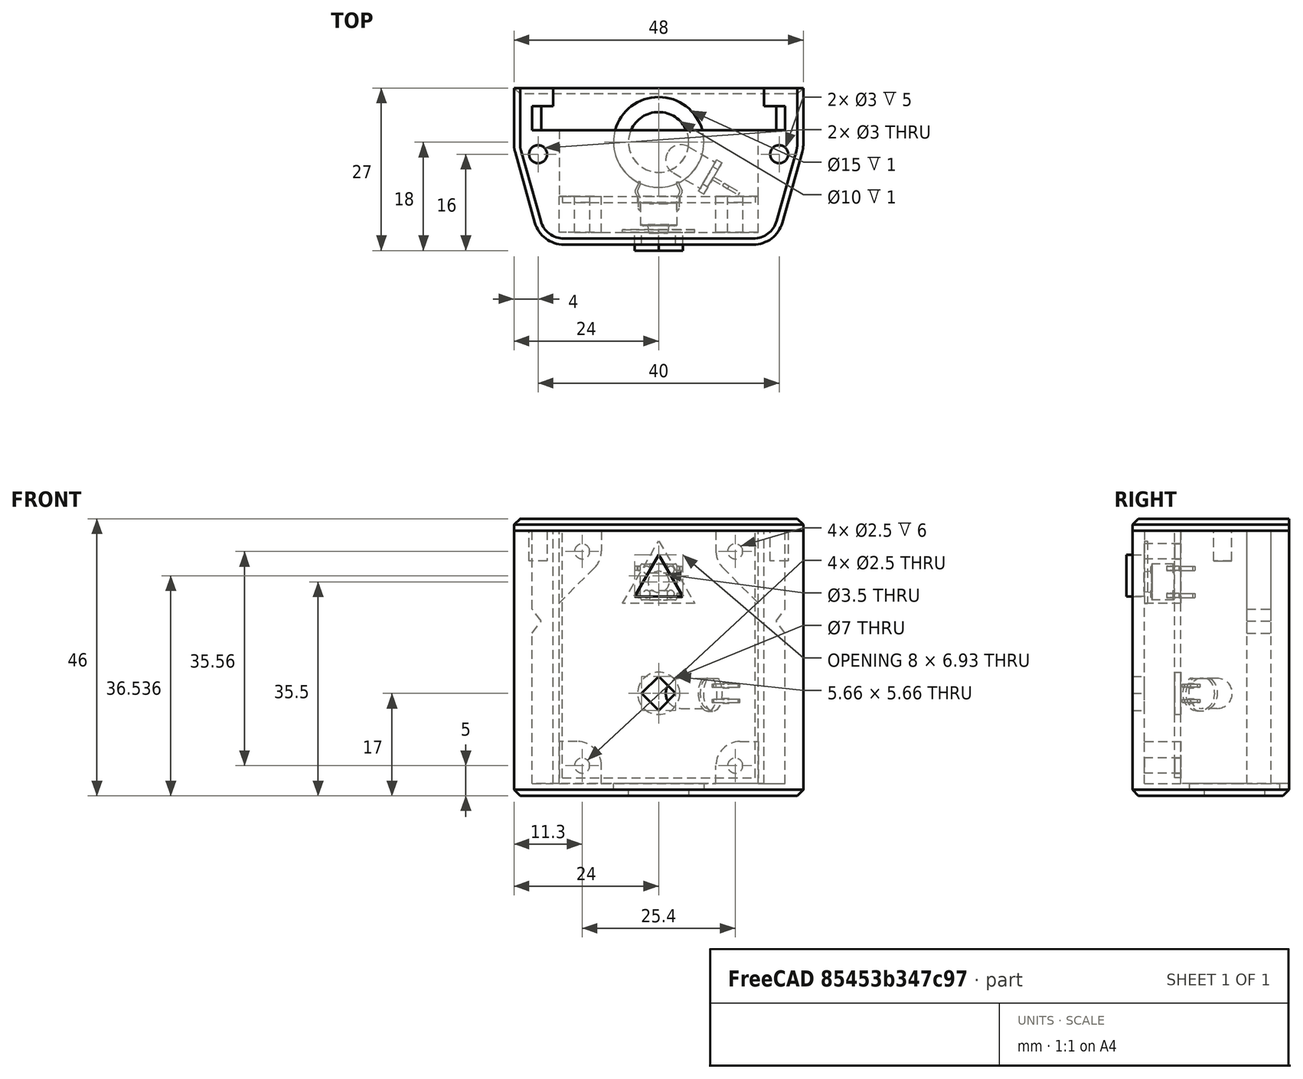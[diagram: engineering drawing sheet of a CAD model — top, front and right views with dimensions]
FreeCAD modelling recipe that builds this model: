
FCSTD DOCUMENT  (FreeCAD 2023.114R26244 +5346 (Git))
Label: avvisoBoule
License: All rights reserved
LicenseURL: http://en.wikipedia.org/wiki/All_rights_reserved
objects: Sketcher::SketchObject×12, PartDesign::Pad×7, PartDesign::Pocket×5, Part::SubShapeBinder×4, PartDesign::Body×4, App::Part×4, PartDesign::Fillet×3, Part::Feature×3, PartDesign::Chamfer×2, PartDesign::AdditiveBox×1, Mesh::Feature×1
note: 89 computed .brp shape members not serialized (recipe doc carries the construction recipe); baked Part::Feature solids carry a one-line shape summary decoded from their .brp

FEATURE [Sketcher::SketchObject] Sketch
  ArcFitTolerance = 1e-06
  AttachmentSupport = -> [XY_Plane]
  ExternalBSplineMaxDegree = 5
  ExternalBSplineTolerance = 0.0001
  FullyConstrained = true
  InternalTolerance = 1e-06
  InvalidShape = false
  MakeInternals = false
  MapMode = 5
  Support = -> [XY_Plane]
  TreeRank = 18
  ValidateShape = true
  sketch-geometry (18):
    g0: LineSegment StartX=-17.5 StartY=4 StartZ=0 EndX=-17.5 EndY=7 EndZ=0
    g1: LineSegment StartX=-17.5 StartY=7 StartZ=0 EndX=-24 EndY=7 EndZ=0
    g2: LineSegment StartX=-24 StartY=7 StartZ=0 EndX=-24 EndY=-3 EndZ=0
    g3: LineSegment StartX=24 StartY=-3 StartZ=0 EndX=24 EndY=7 EndZ=0
    g4: LineSegment StartX=24 StartY=7 StartZ=0 EndX=17.5 EndY=7 EndZ=0
    g5: LineSegment StartX=17.5 StartY=7 StartZ=0 EndX=17.5 EndY=4 EndZ=0
    g6: LineSegment StartX=17.5 StartY=4 StartZ=0 EndX=21 EndY=4 EndZ=0
    g7: LineSegment StartX=21 StartY=4 StartZ=0 EndX=21 EndY=0 EndZ=0
    g8: LineSegment StartX=-21 StartY=0 StartZ=0 EndX=-21 EndY=4 EndZ=0
    g9: LineSegment StartX=-21 StartY=4 StartZ=0 EndX=-17.5 EndY=4 EndZ=0
    g10: LineSegment StartX=-19.5 StartY=-19 StartZ=0 EndX=19.5 EndY=-19 EndZ=0
    g11: LineSegment StartX=-16.5 StartY=0 StartZ=0 EndX=-16.5 EndY=-17 EndZ=0
    g12: LineSegment StartX=-16.5 StartY=-17 StartZ=0 EndX=16.5 EndY=-17 EndZ=0
    g13: LineSegment StartX=16.5 StartY=-17 StartZ=0 EndX=16.5 EndY=0 EndZ=0
    g14: LineSegment StartX=-16.5 StartY=0 StartZ=0 EndX=-21 EndY=0 EndZ=0
    g15: LineSegment StartX=16.5 StartY=0 StartZ=0 EndX=21 EndY=0 EndZ=0
    g16: LineSegment StartX=-24 StartY=-3 StartZ=0 EndX=-19.5 EndY=-19 EndZ=0
    g17: LineSegment StartX=19.5 StartY=-19 StartZ=0 EndX=24 EndY=-3 EndZ=0
  constraints (51):
    c: Vertical(g0)
    c: Coincident(g0,g1)
    c: Coincident(g1,g2)
    c: Vertical(g2)
    c: Coincident(g3,g4)
    c: Coincident(g4,g5)
    c: Coincident(g5,g6)
    c: Coincident(g6,g7)
    c: Coincident(g14,g8)
    c: Vertical(g8)
    c: Coincident(g8,g9)
    c: Coincident(g9,g0)
    c: Horizontal(g9)
    c: Horizontal(g1)
    c: Horizontal(g4)
    c: Horizontal(g6)
    c: Vertical(g3)
    c: Vertical(g7)
    c: Vertical(g5)
    c: Equal(g4,g1)
    c: Equal(g6,g9)
    c: Equal(g0,g5)
    c: Symmetric(g0,g4,g-2)
    c: PointOnObject(g14,g-1)
    c: DistanceY(g2,g14) = 3
    c: DistanceY(g8,g8) = 4
    c: DistanceX(g0,g4) = 35
    c: DistanceX(g14,g7) = 42
    c: DistanceX(g1,g8) = 3
    c: DistanceY(g0,g0) = 3
    c: Symmetric(g10,g10,g-2)
    c: Vertical(g11)
    c: Coincident(g11,g12)
    c: Coincident(g12,g13)
    c: Vertical(g13)
    c: Coincident(g14,g11)
    c: Symmetric(g11,g12,g-2)
    c: Coincident(g15,g13)
    c: Coincident(g15,g7)
    c: Coincident(g16,g2)
    c: Coincident(g16,g10)
    c: Coincident(g17,g10)
    c: Coincident(g17,g3)
    c: DistanceX(g14,g14) = 4.5
    c: DistanceY(g11,g11) = 17
    c: Horizontal(g14)
    c: DistanceY(g10,g11) = 2
    c: DistanceX(g10,g11) = 3
    c: Equal(g7,g8)
    c: Horizontal(g15)
    c: Equal(g2,g3)
FEATURE [PartDesign::Pad] Pad
  AddSubType = 0
  AlongSketchNormal = false
  AutoTaperInnerAngle = true
  CheckUpToFaceLimits = true
  ClaimChildren = false
  Direction = (0,0,1)
  Fit = 0
  FitJoin = 0
  InnerFit = 0
  InnerFitJoin = 0
  InvalidShape = false
  Length = 42
  Length2 = 100
  Linearize = true
  NewSolid = false
  Profile = -> Sketch
  Suppress = false
  TaperInnerAngle = 0
  TaperInnerAngleRev = 0
  TreeRank = 19
  Type = 0
  ValidateShape = true
  _ProfileBasedVersion = 1
FEATURE [Sketcher::SketchObject] Sketch001
  ArcFitTolerance = 1e-06
  AttachmentSupport = -> [Pad]
  ExternalBSplineMaxDegree = 5
  ExternalBSplineTolerance = 0.0001
  ExternalGeometry = -> [Pad]
  FullyConstrained = true
  InternalTolerance = 1e-06
  InvalidShape = false
  MakeInternals = false
  MapMode = 5
  Placement = pos=(0,0,0) rot=(1,0,0;3.14159rad)
  Support = -> [Pad]
  TreeRank = 20
  ValidateShape = true
  sketch-geometry (6):
    g0: LineSegment StartX=-19.5 StartY=19 StartZ=0 EndX=19.5 EndY=19 EndZ=0
    g1: LineSegment StartX=19.5 StartY=19 StartZ=0 EndX=24 EndY=3 EndZ=0
    g2: LineSegment StartX=24 StartY=3 StartZ=0 EndX=24 EndY=-7 EndZ=0
    g3: LineSegment StartX=24 StartY=-7 StartZ=0 EndX=-24 EndY=-7 EndZ=0
    g4: LineSegment StartX=-24 StartY=-7 StartZ=0 EndX=-24 EndY=3 EndZ=0
    g5: LineSegment StartX=-24 StartY=3 StartZ=0 EndX=-19.5 EndY=19 EndZ=0
  constraints (12):
    c: Coincident(g-3,g0)
    c: Coincident(g0,g-3)
    c: Coincident(g0,g1)
    c: Coincident(g1,g-5)
    c: Coincident(g1,g2)
    c: Coincident(g2,g-5)
    c: Coincident(g2,g3)
    c: Coincident(g3,g-4)
    c: Coincident(g3,g4)
    c: Coincident(g4,g-4)
    c: Coincident(g4,g5)
    c: Coincident(g5,g0)
FEATURE [PartDesign::Pad] Pad001
  AddSubType = 0
  AlongSketchNormal = false
  AutoTaperInnerAngle = true
  BaseFeature = -> Pad
  CheckUpToFaceLimits = true
  ClaimChildren = false
  Direction = (0,0,-1)
  Fit = 0
  FitJoin = 0
  InnerFit = 0
  InnerFitJoin = 0
  InvalidShape = false
  Length = 2
  Length2 = 100
  Linearize = true
  NewSolid = false
  Profile = -> Sketch001
  Suppress = false
  TaperInnerAngle = 0
  TaperInnerAngleRev = 0
  TreeRank = 21
  Type = 0
  ValidateShape = true
  _ProfileBasedVersion = 1
FEATURE [Sketcher::SketchObject] Sketch002
  ArcFitTolerance = 1e-06
  AttachmentSupport = -> [Pad001]
  ExternalBSplineMaxDegree = 5
  ExternalBSplineTolerance = 0.0001
  FullyConstrained = true
  InternalTolerance = 1e-06
  InvalidShape = false
  MakeInternals = false
  MapMode = 5
  Placement = pos=(0,-19,0) rot=(1,0,0;1.5708rad)
  Support = -> [Pad001]
  TreeRank = 22
  ValidateShape = true
  sketch-geometry (7):
    g0: LineSegment StartX=-4 StartY=31.0718 StartZ=0 EndX=-4.459e-13 EndY=38 EndZ=0
    g1: LineSegment StartX=-4.46e-13 StartY=38 StartZ=0 EndX=4 EndY=31.0718 EndZ=0
    g2: LineSegment StartX=-2.82843 StartY=15 StartZ=0 EndX=0 EndY=17.8284 EndZ=0
    g3: LineSegment StartX=0 StartY=17.8284 StartZ=0 EndX=2.82843 EndY=15 EndZ=0
    g4: LineSegment StartX=2.82843 StartY=15 StartZ=0 EndX=0 EndY=12.1716 EndZ=0
    g5: LineSegment StartX=0 StartY=12.1716 StartZ=0 EndX=-2.82843 EndY=15 EndZ=0
    g6: LineSegment StartX=-4 StartY=31.0718 StartZ=0 EndX=4 EndY=31.0718 EndZ=0
  constraints (20):
    c: Coincident(g0,g1)
    c: Symmetric(g0,g1,g-2)
    c: Angle(g0,g1) = 1.0472
    c: Coincident(g2,g3)
    c: Coincident(g3,g4)
    c: Coincident(g4,g5)
    c: Coincident(g5,g2)
    c: Parallel(g5,g3)
    c: Parallel(g2,g4)
    c: PointOnObject(g2,g-2)
    c: PointOnObject(g4,g-2)
    c: Horizontal(g2,g3)
    c: Angle(g2,g3) = 1.5708
    c: DistanceY(g2) = 15
    c: Distance(g4) = 4
    c: Distance(g0) = 8
    c: Equal(g1,g0)
    c: Coincident(g6,g0)
    c: Coincident(g6,g1)
    c: DistanceY(g0) = 38
FEATURE [PartDesign::Pocket] Pocket
  AddSubType = 1
  AutoTaperInnerAngle = true
  BaseFeature = -> Pad001
  CheckUpToFaceLimits = true
  ClaimChildren = false
  Fit = 0
  FitJoin = 0
  InnerFit = 0
  InnerFitJoin = 0
  InvalidShape = false
  Length = 5
  Length2 = 100
  Linearize = true
  NewSolid = false
  Profile = -> Sketch002
  Suppress = false
  TaperInnerAngle = 0
  TaperInnerAngleRev = 0
  TreeRank = 23
  Type = 2
  ValidateShape = true
  _ProfileBasedVersion = 1
  _Version = 1
FEATURE [Sketcher::SketchObject] Sketch003
  ArcFitTolerance = 1e-06
  AttachmentSupport = -> [Pocket]
  ExternalBSplineMaxDegree = 5
  ExternalBSplineTolerance = 0.0001
  ExternalGeometry = -> [Pocket]
  FullyConstrained = true
  InternalTolerance = 1e-06
  InvalidShape = false
  MakeInternals = false
  MapMode = 5
  Placement = pos=(0,0,0) rot=(0,0.707107,0.707107;3.14159rad)
  Support = -> [Pocket]
  TreeRank = 24
  ValidateShape = true
  sketch-geometry (6):
    g0: LineSegment StartX=-21 StartY=29 StartZ=0 EndX=-21 EndY=25 EndZ=0
    g1: LineSegment StartX=-21 StartY=25 StartZ=0 EndX=-19.5 EndY=27 EndZ=0
    g2: LineSegment StartX=-19.5 StartY=27 StartZ=0 EndX=-21 EndY=29 EndZ=0
    g3: LineSegment StartX=21 StartY=29 StartZ=0 EndX=21 EndY=25 EndZ=0
    g4: LineSegment StartX=21 StartY=25 StartZ=0 EndX=19.5 EndY=27 EndZ=0
    g5: LineSegment StartX=19.5 StartY=27 StartZ=0 EndX=21 EndY=29 EndZ=0
  constraints (17):
    c: PointOnObject(g0,g-3)
    c: PointOnObject(g0,g-3)
    c: Coincident(g0,g1)
    c: Coincident(g1,g2)
    c: Coincident(g2,g0)
    c: PointOnObject(g3,g-4)
    c: PointOnObject(g3,g-4)
    c: Coincident(g3,g4)
    c: Coincident(g4,g5)
    c: Coincident(g5,g3)
    c: Horizontal(g0,g3)
    c: Equal(g0,g3)
    c: Symmetric(g1,g4,g-2)
    c: DistanceX(g0,g1) = 1.5
    c: DistanceY(g0,g0) = 4
    c: DistanceY(g0,g1) = 2
    c: DistanceY(g0) = 25
FEATURE [PartDesign::Pad] Pad002
  AddSubType = 0
  AlongSketchNormal = false
  AutoTaperInnerAngle = true
  BaseFeature = -> Pocket
  CheckUpToFaceLimits = true
  ClaimChildren = false
  Direction = (0,1,-2e-16)
  Fit = 0
  FitJoin = 0
  InnerFit = 0
  InnerFitJoin = 0
  InvalidShape = false
  Length = 10
  Length2 = 100
  Linearize = true
  NewSolid = false
  Profile = -> Sketch003
  Suppress = false
  TaperInnerAngle = 0
  TaperInnerAngleRev = 0
  TreeRank = 25
  Type = 3
  UpToFace = -> Pocket [Face10]
  ValidateShape = true
  _ProfileBasedVersion = 1
FEATURE [PartDesign::Fillet] Fillet
  AddSubType = 0
  Base = -> Pad002 [Edge72,Edge74,Edge77,Edge85]
  BaseFeature = -> Pad002
  InvalidShape = false
  NewSolid = false
  Radius = 5
  SupportTransform = false
  Suppress = false
  TreeRank = 26
  ValidateShape = true
FEATURE [Sketcher::SketchObject] Sketch004
  ArcFitTolerance = 1e-06
  AttachmentSupport = -> [Fillet]
  ExternalBSplineMaxDegree = 5
  ExternalBSplineTolerance = 0.0001
  ExternalGeometry = -> [Fillet]
  FullyConstrained = true
  InternalTolerance = 1e-06
  InvalidShape = false
  MakeInternals = false
  MapMode = 5
  Placement = pos=(0,-17,0) rot=(0,0.707107,0.707107;3.14159rad)
  Support = -> [Fillet]
  TreeRank = 27
  ValidateShape = true
  sketch-geometry (20):
    g0: LineSegment StartX=-16.5 StartY=42 StartZ=0 EndX=-9.5 EndY=42 EndZ=0
    g1: LineSegment StartX=-9.5 StartY=42 StartZ=0 EndX=-9.5 EndY=37 EndZ=0
    g2: LineSegment StartX=-16.5 StartY=30 StartZ=0 EndX=-16.5 EndY=42 EndZ=0
    g3: LineSegment StartX=16.5 StartY=42 StartZ=0 EndX=9.5 EndY=42 EndZ=0
    g4: LineSegment StartX=9.5 StartY=42 StartZ=0 EndX=9.5 EndY=37 EndZ=0
    g5: LineSegment StartX=16.5 StartY=30 StartZ=0 EndX=16.5 EndY=42 EndZ=0
    g6: LineSegment StartX=-16.5 StartY=0 StartZ=0 EndX=-9.5 EndY=0 EndZ=0
    g7: LineSegment StartX=-9.5 StartY=0 StartZ=0 EndX=-9.5 EndY=7 EndZ=0
    g8: LineSegment StartX=-9.5 StartY=7 StartZ=0 EndX=-16.5 EndY=7 EndZ=0
    g9: LineSegment StartX=-16.5 StartY=7 StartZ=0 EndX=-16.5 EndY=0 EndZ=0
    g10: LineSegment StartX=16.5 StartY=0 StartZ=0 EndX=9.5 EndY=0 EndZ=0
    g11: LineSegment StartX=9.5 StartY=0 StartZ=0 EndX=9.5 EndY=7 EndZ=0
    g12: LineSegment StartX=9.5 StartY=7 StartZ=0 EndX=16.5 EndY=7 EndZ=0
    g13: LineSegment StartX=16.5 StartY=7 StartZ=0 EndX=16.5 EndY=0 EndZ=0
    g14: Circle CenterX=-12.7 CenterY=38.56 CenterZ=0 NormalX=0 NormalY=0 NormalZ=1 AngleXU=0 Radius=1.25
    g15: Circle CenterX=-12.7 CenterY=3 CenterZ=0 NormalX=0 NormalY=0 NormalZ=1 AngleXU=0 Radius=1.25
    g16: Circle CenterX=12.7 CenterY=3 CenterZ=0 NormalX=0 NormalY=0 NormalZ=1 AngleXU=0 Radius=1.25
    g17: Circle CenterX=12.7 CenterY=38.56 CenterZ=0 NormalX=0 NormalY=0 NormalZ=1 AngleXU=0 Radius=1.25
    g18: LineSegment StartX=-16.5 StartY=30 StartZ=0 EndX=-9.5 EndY=37 EndZ=0
    g19: LineSegment StartX=9.5 StartY=37 StartZ=0 EndX=16.5 EndY=30 EndZ=0
  constraints (55):
    c: Coincident(g0,g1)
    c: Coincident(g2,g0)
    c: Horizontal(g0)
    c: Vertical(g1)
    c: Vertical(g2)
    c: Coincident(g3,g4)
    c: Coincident(g5,g3)
    c: Horizontal(g3)
    c: Vertical(g4)
    c: Vertical(g5)
    c: Coincident(g6,g7)
    c: Coincident(g7,g8)
    c: Coincident(g8,g9)
    c: Coincident(g9,g6)
    c: Horizontal(g6)
    c: Horizontal(g8)
    c: Vertical(g7)
    c: Vertical(g9)
    c: Coincident(g10,g11)
    c: Coincident(g11,g12)
    c: Coincident(g12,g13)
    c: Coincident(g13,g10)
    c: Horizontal(g10)
    c: Horizontal(g12)
    c: Vertical(g11)
    c: Vertical(g13)
    c: Equal(g8,g7)
    c: Equal(g1,g4)
    c: Equal(g12,g11)
    c: DistanceY(g7,g7) = 7
    c: Equal(g14,g17)
    c: Equal(g17,g16)
    c: Equal(g16,g15)
    c: Horizontal(g14,g17)
    c: Vertical(g14,g15)
    c: Diameter(g14) = 2.5
    c: DistanceY(g6,g15) = 3
    c: Vertical(g17,g16)
    c: DistanceX(g14,g17) = 25.4
    c: Symmetric(g16,g15,g-2)
    c: Coincident(g6,g-3)
    c: Coincident(g-3,g10)
    c: Coincident(g0,g-4)
    c: DistanceY(g15,g14) = 35.56
    c: Coincident(g18,g2)
    c: Coincident(g18,g1)
    c: Equal(g5,g2)
    c: Coincident(g3,g-4)
    c: Coincident(g19,g4)
    c: Coincident(g19,g5)
    c: Angle(g18) = 0.785398
    c: Vertical(g0,g7)
    c: Vertical(g3,g11)
    c: DistanceY(g1,g1) = 5
    c: Equal(g12,g8)
FEATURE [PartDesign::Pad] Pad003
  AddSubType = 0
  AlongSketchNormal = false
  AutoTaperInnerAngle = true
  BaseFeature = -> Fillet
  CheckUpToFaceLimits = true
  ClaimChildren = false
  Direction = (0,1,-2e-16)
  Fit = 0
  FitJoin = 0
  InnerFit = 0
  InnerFitJoin = 0
  InvalidShape = false
  Length = 6
  Length2 = 100
  Linearize = true
  NewSolid = false
  Profile = -> Sketch004
  Refine = true
  Suppress = false
  TaperInnerAngle = 0
  TaperInnerAngleRev = 0
  TreeRank = 28
  Type = 0
  ValidateShape = true
  _ProfileBasedVersion = 1
FEATURE [PartDesign::Fillet] Fillet001
  AddSubType = 0
  Base = -> Pad003 [Edge157,Edge154,Edge145,Edge146]
  BaseFeature = -> Pad003
  InvalidShape = false
  NewSolid = false
  Radius = 4
  SupportTransform = false
  Suppress = false
  TreeRank = 29
  ValidateShape = true
FEATURE [Sketcher::SketchObject] Sketch005
  ArcFitTolerance = 1e-06
  AttachmentSupport = -> [Fillet001]
  ExternalBSplineMaxDegree = 5
  ExternalBSplineTolerance = 0.0001
  FullyConstrained = true
  InternalTolerance = 1e-06
  InvalidShape = false
  MakeInternals = false
  MapMode = 5
  Support = -> [Fillet001]
  TreeRank = 30
  ValidateShape = true
  sketch-geometry (1):
    g0: Circle CenterX=0 CenterY=-2 CenterZ=0 NormalX=0 NormalY=0 NormalZ=1 AngleXU=0 Radius=7.5
  constraints (3):
    c: Diameter(g0) = 15
    c: PointOnObject(g0,g-2)
    c: DistanceY(g0) = -2
FEATURE [PartDesign::Pocket] Pocket001
  AddSubType = 1
  AutoTaperInnerAngle = true
  BaseFeature = -> Fillet001
  CheckUpToFaceLimits = true
  ClaimChildren = false
  Fit = 0
  FitJoin = 0
  InnerFit = 0
  InnerFitJoin = 0
  InvalidShape = false
  Length = 1
  Length2 = 100
  Linearize = true
  NewSolid = false
  Profile = -> Sketch005
  Suppress = false
  TaperInnerAngle = 0
  TaperInnerAngleRev = 0
  TreeRank = 31
  Type = 0
  ValidateShape = true
  _ProfileBasedVersion = 1
  _Version = 1
FEATURE [Sketcher::SketchObject] Sketch006
  ArcFitTolerance = 1e-06
  AttachmentSupport = -> [Pocket001]
  ExternalBSplineMaxDegree = 5
  ExternalBSplineTolerance = 0.0001
  ExternalGeometry = -> [Pocket001]
  FullyConstrained = true
  InternalTolerance = 1e-06
  InvalidShape = false
  MakeInternals = false
  MapMode = 5
  Placement = pos=(0,0,-1) rot=(0,0,1;0rad)
  Support = -> [Pocket001]
  TreeRank = 32
  ValidateShape = true
  sketch-geometry (1):
    g0: Circle CenterX=0 CenterY=-2 CenterZ=0 NormalX=0 NormalY=0 NormalZ=1 AngleXU=0 Radius=5
  constraints (2):
    c: Coincident(g0,g-3)
    c: Diameter(g0) = 10
FEATURE [PartDesign::Pocket] Pocket002
  AddSubType = 1
  AutoTaperInnerAngle = true
  BaseFeature = -> Pocket001
  CheckUpToFaceLimits = true
  ClaimChildren = false
  Fit = 0
  FitJoin = 0
  InnerFit = 0
  InnerFitJoin = 0
  InvalidShape = false
  Length = 5
  Length2 = 100
  Linearize = true
  NewSolid = false
  Profile = -> Sketch006
  Suppress = false
  TaperInnerAngle = 0
  TaperInnerAngleRev = 0
  TreeRank = 33
  Type = 2
  ValidateShape = true
  _ProfileBasedVersion = 1
  _Version = 1
FEATURE [PartDesign::AdditiveBox] Box
  AddSubType = 0
  AttacherType = Attacher::AttachEngine3D
  AttachmentOffset = pos=(-16,-30,5) rot=(0,0,1;0rad)
  AttachmentSupport = -> [XZ_Plane001]
  Height = 1
  InvalidShape = false
  Length = 32
  MapMode = 2
  NewSolid = false
  Placement = pos=(-16,-5,-30) rot=(1,0,0;1.5708rad)
  Support = -> [XZ_Plane001]
  Suppress = false
  TreeRank = 52
  ValidateShape = true
  Width = 41
FEATURE [Sketcher::SketchObject] Sketch008
  ArcFitTolerance = 1e-06
  AttachmentSupport = -> [Pocket002]
  ExternalBSplineMaxDegree = 5
  ExternalBSplineTolerance = 0.0001
  FullyConstrained = true
  InternalTolerance = 1e-06
  InvalidShape = false
  MakeInternals = false
  MapMode = 5
  Placement = pos=(0,0,42) rot=(0,0,1;0rad)
  Support = -> [Pocket002]
  TreeRank = 58
  ValidateShape = true
  sketch-geometry (2):
    g0: Circle CenterX=-20 CenterY=-4 CenterZ=0 NormalX=0 NormalY=0 NormalZ=1 AngleXU=0 Radius=1.5
    g1: Circle CenterX=20 CenterY=-4 CenterZ=0 NormalX=0 NormalY=0 NormalZ=1 AngleXU=0 Radius=1.5
  constraints (5):
    c: Equal(g1,g0)
    c: Symmetric(g0,g1,g-2)
    c: DistanceX(g1) = 20
    c: DistanceY(g1) = -4
    c: Diameter(g0) = 3
FEATURE [PartDesign::Pocket] Pocket004
  AddSubType = 1
  AutoTaperInnerAngle = true
  BaseFeature = -> Pocket002
  CheckUpToFaceLimits = true
  ClaimChildren = false
  Fit = 0
  FitJoin = 0
  InnerFit = 0
  InnerFitJoin = 0
  InvalidShape = false
  Length = 5
  Length2 = 100
  Linearize = true
  NewSolid = false
  Profile = -> Sketch008
  Suppress = false
  TaperInnerAngle = 0
  TaperInnerAngleRev = 0
  TreeRank = 59
  Type = 0
  ValidateShape = true
  _ProfileBasedVersion = 1
  _Version = 1
FEATURE [Part::SubShapeBinder] Import  label="Import(Pocket004)"
  BindCopyOnChange = 0
  BindMode = 0
  ClaimChildren = false
  Context = -> Part001 [Body001.Import.]
  EdgeTolerance = 1e-06
  FillStyle = 0
  Fuse = false
  InvalidShape = false
  MakeFace = false
  MergeEdges = true
  OffsetFill = false
  OffsetIntersection = false
  OffsetJoinType = 0
  OffsetOpenResult = false
  Outline = false
  PartialLoad = false
  Relative = true
  SplitEdges = false
  Support = -> [Part[Body.Pocket004.]]
  TightBound = false
  TreeRank = 78
  ValidateShape = true
  _Version = 8
FEATURE [Sketcher::SketchObject] Sketch007
  ArcFitTolerance = 1e-06
  AttachmentSupport = -> [Box]
  ExternalBSplineMaxDegree = 5
  ExternalBSplineTolerance = 0.0001
  ExternalGeometry = -> [Import]
  FullyConstrained = true
  InternalTolerance = 1e-06
  InvalidShape = false
  MakeInternals = false
  MapMode = 5
  Placement = pos=(-16,-5,-30) rot=(-1,0,0;1.5708rad)
  Support = -> [Box]
  TreeRank = 53
  ValidateShape = true
  sketch-geometry (5):
    g0: Circle CenterX=16 CenterY=-14 CenterZ=0 NormalX=0 NormalY=0 NormalZ=1 AngleXU=0 Radius=3.5
    g1: Circle CenterX=3.3 CenterY=-2 CenterZ=0 NormalX=0 NormalY=0 NormalZ=1 AngleXU=0 Radius=1.25
    g2: Circle CenterX=28.7 CenterY=-2 CenterZ=0 NormalX=0 NormalY=0 NormalZ=1 AngleXU=0 Radius=1.25
    g3: Circle CenterX=28.7 CenterY=-37.56 CenterZ=0 NormalX=0 NormalY=0 NormalZ=1 AngleXU=0 Radius=1.25
    g4: Circle CenterX=3.3 CenterY=-37.56 CenterZ=0 NormalX=0 NormalY=0 NormalZ=1 AngleXU=0 Radius=1.25
  constraints (11):
    c: Vertical(g0,g-7)
    c: Horizontal(g0,g-7)
    c: Diameter(g0) = 7
    c: Coincident(g1,g-4)
    c: Coincident(g2,g-3)
    c: Coincident(g3,g-6)
    c: Coincident(g4,g-5)
    c: Equal(g4,g3)
    c: Equal(g3,g2)
    c: Equal(g2,g1)
    c: Equal(g1,g-4)
FEATURE [PartDesign::Pocket] Pocket005
  AddSubType = 1
  AutoTaperInnerAngle = true
  BaseFeature = -> Box
  CheckUpToFaceLimits = true
  ClaimChildren = false
  Fit = 0
  FitJoin = 0
  InnerFit = 0
  InnerFitJoin = 0
  InvalidShape = false
  Length = 0
  Length2 = 100
  Linearize = true
  NewSolid = false
  Profile = -> Sketch007
  Suppress = false
  TaperInnerAngle = 0
  TaperInnerAngleRev = 0
  TreeRank = 80
  Type = 2
  ValidateShape = true
  _ProfileBasedVersion = 1
  _Version = 1
FEATURE [PartDesign::Body] Body001
  AutoGroupSolids = false
  ClaimAllChildren = false
  ExportMode = 0
  Group = -> [Box,Sketch007,Import,Pocket005]
  InvalidShape = false
  Origin = -> Origin003
  Placement = pos=(0,-6,31) rot=(0,0,1;0rad)
  Tip = -> Pocket005
  TreeRank = 50
  ValidateShape = true
  _ExportChildren = -> [Box,Import,Pocket005]
  _GroupVersion = 1
FEATURE [Part::Feature] DIP16
  InvalidShape = false
  Placement = pos=(0,-10,7) rot=(1,0,0;1.5708rad)
  TreeRank = 81
  ValidateShape = true
  shape: bbox 19.96 x 7.3 x 7.87 mm, 220 faces, 0 solids (baked)
FEATURE [Part::Feature] Compound  label="5mmLED"
  InvalidShape = false
  Placement = pos=(9,-8,15) rot=(-0.694747,0.186157,0.694747;2.77349rad)
  TreeRank = 82
  ValidateShape = true
  shape: bbox 12.28 x 8.292 x 5.5 mm, 36 faces, 3 solids (baked)
FEATURE [Part::Feature] Feature  label="A06-5.0"
  InvalidShape = false
  Placement = pos=(-3,-12,30.5) rot=(1,0,0;1.5708rad)
  TreeRank = 83
  ValidateShape = true
  shape: bbox 7.835 x 8.5 x 6 mm, 109 faces, 11 solids (baked)
FEATURE [Part::SubShapeBinder] Import001  label="Import001(Pocket004)"
  BindCopyOnChange = 0
  BindMode = 0
  ClaimChildren = false
  Context = -> Part003 [Body003.Import001.]
  EdgeTolerance = 1e-06
  FillStyle = 0
  Fuse = false
  InvalidShape = false
  MakeFace = false
  MergeEdges = true
  OffsetFill = false
  OffsetIntersection = false
  OffsetJoinType = 0
  OffsetOpenResult = false
  Outline = false
  PartialLoad = false
  Relative = true
  SplitEdges = false
  Support = -> [Part[Body.Pocket004.]]
  TightBound = false
  TreeRank = 103
  ValidateShape = true
  _Version = 8
FEATURE [PartDesign::Chamfer] Chamfer
  AddSubType = 0
  Angle = 45
  Base = -> Pocket004 [Edge178,Edge123]
  BaseFeature = -> Pocket004
  ChamferType = 0
  FlipDirection = false
  InvalidShape = false
  NewSolid = false
  Size = 1
  Size2 = 1
  SupportTransform = false
  Suppress = false
  TreeRank = 108
  ValidateShape = true
FEATURE [PartDesign::Body] Body
  AutoGroupSolids = false
  ClaimAllChildren = false
  ExportMode = 0
  Group = -> [Sketch,Pad,Sketch001,Pad001,Sketch002,Pocket,Sketch003,Pad002,Fillet,Sketch004,Pad003,Fillet001,Sketch005,Pocket001,Sketch006,Pocket002,Sketch008,Pocket004,Chamfer]
  InvalidShape = false
  Origin = -> Origin001
  Tip = -> Chamfer
  TreeRank = 17
  ValidateShape = true
  _ExportChildren = -> [Pad,Pad001,Pocket,Pad002,Fillet,Pad003,Fillet001,Pocket001,Pocket002,Pocket004,Chamfer]
  _GroupVersion = 1
FEATURE [App::Part] Part  label="scatola"
  ClaimAllChildren = false
  ExportMode = 1
  Group = -> [Body]
  Origin = -> Origin
  TreeRank = 5
  _ExportChildren = -> [Body]
  _GroupVersion = 1
FEATURE [Mesh::Feature] _20mm_coin_holder  label="20mm_coin_holder"
  Placement = pos=(-12.5,-14.5,19) rot=(0,0,1;0rad)
  TreeRank = 133
FEATURE [App::Part] Part001  label="scheda"
  ClaimAllChildren = false
  ExportMode = 1
  Group = -> [Body001,DIP16,Compound,Feature,_20mm_coin_holder]
  Origin = -> Origin002
  Placement = pos=(0,1,0) rot=(0,0,1;0rad)
  TreeRank = 38
  _ExportChildren = -> [Body001,DIP16,Compound,Feature,_20mm_coin_holder]
  _GroupVersion = 1
FEATURE [Part::SubShapeBinder] Import003  label="Import003(Chamfer)"
  BindCopyOnChange = 0
  BindMode = 0
  ClaimChildren = false
  Context = -> Part003 [Body003.Import003.]
  EdgeTolerance = 1e-06
  FillStyle = 0
  Fuse = false
  InvalidShape = false
  MakeFace = false
  MergeEdges = true
  OffsetFill = false
  OffsetIntersection = false
  OffsetJoinType = 0
  OffsetOpenResult = false
  Outline = false
  PartialLoad = false
  Relative = true
  SplitEdges = false
  Support = -> [Part[Body.Chamfer.]]
  TightBound = false
  TreeRank = 134
  ValidateShape = true
  _Version = 8
FEATURE [Sketcher::SketchObject] Sketch010
  ArcFitTolerance = 1e-06
  AttachmentSupport = -> [Import001]
  ExternalBSplineMaxDegree = 5
  ExternalBSplineTolerance = 0.0001
  ExternalGeometry = -> [Import003]
  FullyConstrained = true
  InternalTolerance = 1e-06
  InvalidShape = false
  MakeInternals = false
  MapMode = 5
  Placement = pos=(0,-17,0) rot=(0,0.707107,0.707107;3.14159rad)
  Support = -> [Import001]
  TreeRank = 104
  ValidateShape = true
  sketch-geometry (4):
    g0: LineSegment StartX=0 StartY=40.3094 StartZ=0 EndX=-6 EndY=29.9171 EndZ=0
    g1: LineSegment StartX=6 StartY=29.9171 StartZ=0 EndX=-9e-16 EndY=40.3094 EndZ=0
    g2: LineSegment StartX=-6 StartY=29.9171 StartZ=0 EndX=6 EndY=29.9171 EndZ=0
    g3: LineSegment [constr] StartX=-6 StartY=29.9171 StartZ=0 EndX=3 EndY=35.1132 EndZ=0
  constraints (12):
    c: PointOnObject(g0,g-2)
    c: Coincident(g1,g0)
    c: Equal(g1,g0)
    c: Angle(g0,g1) = 1.0472
    c: Distance(g0) = 12
    c: Coincident(g2,g0)
    c: Coincident(g2,g1)
    c: Horizontal(g2)
    c: Coincident(g3,g0)
    c: PointOnObject(g3,g1)
    c: Angle(g3) = 0.523599
    c: PointOnObject(g-3,g3)
FEATURE [PartDesign::Pad] Pad004
  AddSubType = 0
  AlongSketchNormal = false
  AutoTaperInnerAngle = true
  CheckUpToFaceLimits = true
  ClaimChildren = false
  Direction = (0,1,-2e-16)
  Fit = 0
  FitJoin = 0
  InnerFit = 0
  InnerFitJoin = 0
  InvalidShape = false
  Length = 0.5
  Length2 = 100
  Linearize = true
  NewSolid = false
  Profile = -> Sketch010
  Suppress = false
  TaperInnerAngle = 0
  TaperInnerAngleRev = 0
  TreeRank = 105
  Type = 0
  ValidateShape = true
  _ProfileBasedVersion = 1
FEATURE [Sketcher::SketchObject] Sketch011
  ArcFitTolerance = 1e-06
  AttachmentSupport = -> [Pad004]
  ExternalBSplineMaxDegree = 5
  ExternalBSplineTolerance = 0.0001
  ExternalGeometry = -> [Pad004]
  FullyConstrained = true
  InternalTolerance = 1e-06
  InvalidShape = false
  MakeInternals = false
  MapMode = 5
  Placement = pos=(0,-17,5.8e-15) rot=(1,0,0;1.5708rad)
  Support = -> [Pad004]
  TreeRank = 106
  ValidateShape = true
  sketch-geometry (4):
    g0: LineSegment StartX=0 StartY=38 StartZ=0 EndX=-4 EndY=31.0718 EndZ=0
    g1: LineSegment StartX=4 StartY=31.0718 StartZ=0 EndX=0 EndY=38 EndZ=0
    g2: LineSegment StartX=-4 StartY=31.0718 StartZ=0 EndX=4 EndY=31.0718 EndZ=0
    g3: LineSegment [constr] StartX=-6 StartY=29.9171 StartZ=0 EndX=2 EndY=34.5359 EndZ=0
  constraints (12):
    c: PointOnObject(g0,g-2)
    c: Coincident(g1,g0)
    c: Angle(g0,g1) = 1.0472
    c: Distance(g0) = 8
    c: Coincident(g2,g0)
    c: Coincident(g2,g1)
    c: Horizontal(g2)
    c: Equal(g2,g1)
    c: Coincident(g3,g-3)
    c: PointOnObject(g3,g1)
    c: Angle(g3) = 0.523599
    c: PointOnObject(g0,g3)
FEATURE [PartDesign::Pad] Pad005
  AddSubType = 0
  AlongSketchNormal = false
  AutoTaperInnerAngle = true
  BaseFeature = -> Pad004
  CheckUpToFaceLimits = true
  ClaimChildren = false
  Direction = (0,-1,4e-16)
  Fit = 0
  FitJoin = 0
  InnerFit = 0
  InnerFitJoin = 0
  InvalidShape = false
  Length = 3
  Length2 = 100
  Linearize = true
  NewSolid = false
  Profile = -> Sketch011
  Suppress = false
  TaperInnerAngle = 0
  TaperInnerAngleRev = 0
  TreeRank = 107
  Type = 0
  ValidateShape = true
  _ProfileBasedVersion = 1
FEATURE [PartDesign::Body] Body003
  AutoGroupSolids = false
  ClaimAllChildren = false
  ExportMode = 0
  Group = -> [Import001,Sketch010,Pad004,Sketch011,Pad005,Import003]
  InvalidShape = false
  Origin = -> Origin007
  Tip = -> Pad005
  TreeRank = 100
  ValidateShape = true
  _ExportChildren = -> [Import001,Pad004,Pad005,Import003]
  _GroupVersion = 1
FEATURE [App::Part] Part003  label="tasto"
  ClaimAllChildren = false
  ExportMode = 1
  Group = -> [Body003]
  Origin = -> Origin006
  TreeRank = 88
  _ExportChildren = -> [Body003]
  _GroupVersion = 1
FEATURE [Part::SubShapeBinder] Import004  label="Import004(Chamfer)"
  BindCopyOnChange = 0
  BindMode = 0
  ClaimChildren = false
  Context = -> Part005 [Body005.Import004.]
  EdgeTolerance = 1e-06
  FillStyle = 0
  Fuse = false
  InvalidShape = false
  MakeFace = false
  MergeEdges = true
  OffsetFill = false
  OffsetIntersection = false
  OffsetJoinType = 0
  OffsetOpenResult = false
  Outline = false
  PartialLoad = false
  Relative = true
  SplitEdges = false
  Support = -> [Part[Body.Chamfer.]]
  TightBound = false
  TreeRank = 168
  ValidateShape = true
  _Version = 8
FEATURE [Sketcher::SketchObject] Sketch013
  ArcFitTolerance = 1e-06
  AttachmentSupport = -> [Import004]
  ExternalBSplineMaxDegree = 5
  ExternalBSplineTolerance = 0.0001
  ExternalGeometry = -> [Import004]
  FullyConstrained = true
  InternalTolerance = 1e-06
  InvalidShape = false
  MakeInternals = false
  MapMode = 5
  Placement = pos=(0,0,42) rot=(0,0,1;0rad)
  Support = -> [Import004]
  TreeRank = 169
  ValidateShape = true
  sketch-geometry (16):
    g0: LineSegment StartX=-21 StartY=0 StartZ=0 EndX=-21 EndY=4 EndZ=0
    g1: LineSegment StartX=-21 StartY=4 StartZ=0 EndX=-17.5 EndY=4 EndZ=0
    g2: LineSegment StartX=-17.5 StartY=4 StartZ=0 EndX=-17.5 EndY=7 EndZ=0
    g3: LineSegment StartX=-17.5 StartY=7 StartZ=0 EndX=-24 EndY=7 EndZ=0
    g4: LineSegment StartX=-24 StartY=7 StartZ=0 EndX=-24 EndY=-3 EndZ=0
    g5: LineSegment StartX=-24 StartY=-3 StartZ=0 EndX=-19.5 EndY=-19 EndZ=0
    g6: LineSegment StartX=24 StartY=7 StartZ=0 EndX=17.5 EndY=7 EndZ=0
    g7: LineSegment StartX=17.5 StartY=7 StartZ=0 EndX=17.5 EndY=4 EndZ=0
    g8: LineSegment StartX=17.5 StartY=4 StartZ=0 EndX=21 EndY=4 EndZ=0
    g9: LineSegment StartX=21 StartY=4 StartZ=0 EndX=21 EndY=0 EndZ=0
    g10: LineSegment StartX=21 StartY=0 StartZ=0 EndX=-21 EndY=0 EndZ=0
    g11: LineSegment StartX=-19.5 StartY=-19 StartZ=0 EndX=19.5 EndY=-19 EndZ=0
    g12: LineSegment StartX=24 StartY=7 StartZ=0 EndX=24 EndY=-3 EndZ=0
    g13: LineSegment StartX=24 StartY=-3 StartZ=0 EndX=19.5 EndY=-19 EndZ=0
    g14: Circle CenterX=-20 CenterY=-4 CenterZ=0 NormalX=0 NormalY=0 NormalZ=1 AngleXU=0 Radius=1.5
    g15: Circle CenterX=20 CenterY=-4 CenterZ=0 NormalX=0 NormalY=0 NormalZ=1 AngleXU=0 Radius=1.5
  constraints (36):
    c: Coincident(g-4,g0)
    c: Coincident(g0,g-7)
    c: Coincident(g0,g1)
    c: PointOnObject(g1,g-7)
    c: Coincident(g1,g2)
    c: Coincident(g2,g-3)
    c: Coincident(g2,g3)
    c: Coincident(g3,g-3)
    c: Coincident(g3,g4)
    c: Vertical(g4)
    c: Coincident(g4,g5)
    c: Coincident(g6,g7)
    c: Coincident(g7,g8)
    c: Coincident(g8,g9)
    c: PointOnObject(g9,g-1)
    c: Coincident(g9,g10)
    c: Coincident(g10,g0)
    c: Vertical(g7)
    c: Vertical(g9)
    c: Symmetric(g2,g6,g-2)
    c: Symmetric(g1,g7,g-2)
    c: Symmetric(g8,g0,g-2)
    c: PointOnObject(g5,g-5)
    c: Symmetric(g6,g3,g-2)
    c: PointOnObject(g4,g-5)
    c: Coincident(g5,g11)
    c: Symmetric(g11,g5,g-2)
    c: PointOnObject(g5,g-6)
    c: Coincident(g12,g13)
    c: Coincident(g13,g11)
    c: Symmetric(g12,g4,g-2)
    c: Coincident(g12,g6)
    c: Coincident(g14,g-8)
    c: Equal(g-8,g14)
    c: Equal(g15,g14)
    c: Symmetric(g15,g14,g-2)
FEATURE [PartDesign::Pad] Pad006
  AddSubType = 0
  AlongSketchNormal = false
  AutoTaperInnerAngle = true
  CheckUpToFaceLimits = true
  ClaimChildren = false
  Direction = (0,0,1)
  Fit = 0
  FitJoin = 0
  InnerFit = 0
  InnerFitJoin = 0
  InvalidShape = false
  Length = 2
  Length2 = 100
  Linearize = true
  NewSolid = false
  Profile = -> Sketch013
  Suppress = false
  TaperInnerAngle = 0
  TaperInnerAngleRev = 0
  TreeRank = 170
  Type = 0
  ValidateShape = true
  _ProfileBasedVersion = 1
FEATURE [PartDesign::Fillet] Fillet002
  AddSubType = 0
  Base = -> Pad006 [Edge38,Edge29,Edge32,Edge35]
  BaseFeature = -> Pad006
  InvalidShape = false
  NewSolid = false
  Radius = 5
  SupportTransform = false
  Suppress = false
  TreeRank = 171
  ValidateShape = true
FEATURE [PartDesign::Chamfer] Chamfer001
  AddSubType = 0
  Angle = 45
  Base = -> Fillet002 [Edge32]
  BaseFeature = -> Fillet002
  ChamferType = 0
  FlipDirection = false
  InvalidShape = false
  NewSolid = false
  Size = 1
  Size2 = 1
  SupportTransform = false
  Suppress = false
  TreeRank = 172
  ValidateShape = true
FEATURE [PartDesign::Body] Body005
  AutoGroupSolids = false
  ClaimAllChildren = false
  ExportMode = 0
  Group = -> [Import004,Sketch013,Pad006,Fillet002,Chamfer001]
  InvalidShape = false
  Origin = -> Origin011
  Tip = -> Chamfer001
  TreeRank = 165
  ValidateShape = true
  _ExportChildren = -> [Import004,Pad006,Fillet002,Chamfer001]
  _GroupVersion = 1
FEATURE [App::Part] Part005  label="tappo"
  ClaimAllChildren = false
  ExportMode = 1
  Group = -> [Body005]
  Origin = -> Origin010
  TreeRank = 153
  _ExportChildren = -> [Body005]
  _GroupVersion = 1
